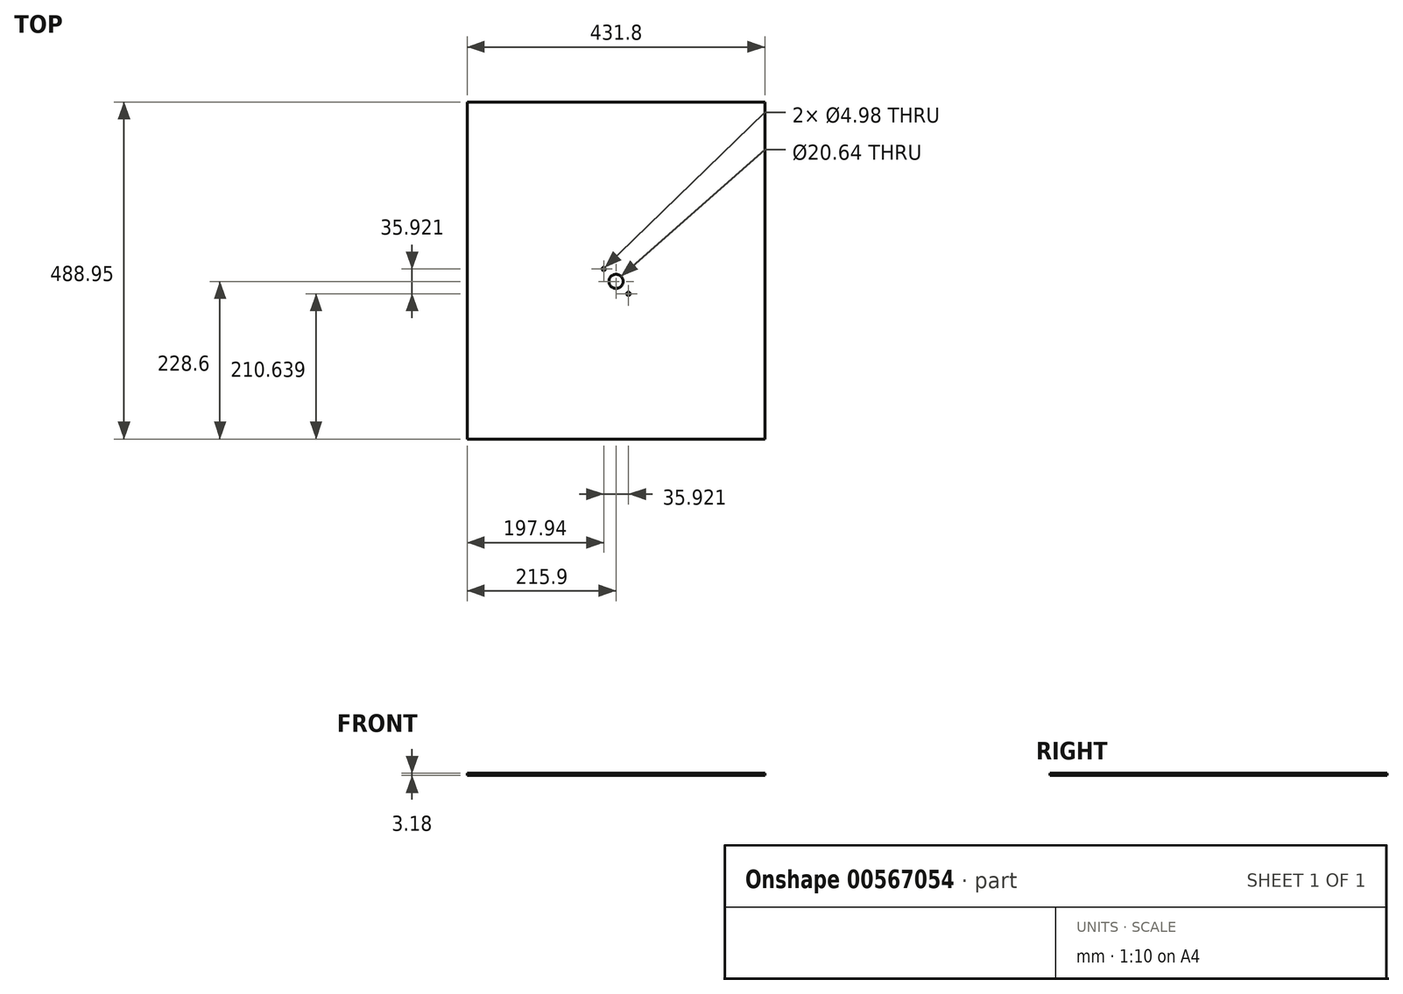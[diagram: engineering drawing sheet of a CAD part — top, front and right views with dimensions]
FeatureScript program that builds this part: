
annotation { "Feature Type Name" : "Feature", "Feature Type Description" : "" }
export const myFeature = defineFeature(function(context is Context, id is Id, definition is map)
    precondition{}
    {
        {
            var Q0;
            Q0=qCreatedBy(makeId("Top.planeOp"),FACE);
            var sketch = newSketch(context, id + "F0", { "sketchPlane" : qUnion([Q0])});
            skPoint(sketch, "E0.middle", {"position": v(0, 15.88) * mm});
            skCircle(sketch, "E1", {"center": v(0, 0) * mm, "radius": 254 * mm, "construction": true});
            skCircle(sketch, "E2", {"center": v(0, 0) * mm, "radius": 10.32 * mm});
            skCircle(sketch, "E3", {"center": v(17.96, -17.96) * mm, "radius": 2.49 * mm});
            skCircle(sketch, "E4", {"center": v(-17.96, 17.96) * mm, "radius": 2.49 * mm});
            skCircle(sketch, "E5", {"center": v(0, 0) * mm, "radius": 25.4 * mm, "construction": true});
            skLineSegment(sketch, "E6", {"start": v(17.96, -17.96) * mm, "end": v(-17.96, 17.96) * mm, "construction": true});
            skLineSegment(sketch, "E7.bottom", {"start": v(-215.9, 260.35) * mm, "end": v(215.9, 260.35) * mm});
            skLineSegment(sketch, "E7.top", {"start": v(-215.9, -228.6) * mm, "end": v(215.9, -228.6) * mm});
            skLineSegment(sketch, "E7.left", {"start": v(-215.9, 260.35) * mm, "end": v(-215.9, -31.75) * mm});
            skLineSegment(sketch, "E7.right", {"start": v(215.9, 260.35) * mm, "end": v(215.9, -228.6) * mm});
            skLineSegment(sketch, "E8", {"start": v(0, -231.78) * mm, "end": v(0, -228.6) * mm, "construction": true});
            skLineSegment(sketch, "E9", {"start": v(0, 260.35) * mm, "end": v(0, 263.53) * mm, "construction": true});
            skLineSegment(sketch, "E10", {"start": v(-219.08, 117.48) * mm, "end": v(-215.9, 117.48) * mm, "construction": true});
            skCircle(sketch, "E11", {"center": v(0, 0) * mm, "radius": 203.2 * mm, "construction": true});
            skLineSegment(sketch, "E12", {"start": v(-215.9, -31.75) * mm, "end": v(-215.9, -228.6) * mm});
            skPoint(sketch, "E13.orphan", {"position": v(219.08, -231.78) * mm});
            skPoint(sketch, "E14.orphan", {"position": v(219.08, 263.53) * mm});
            skPoint(sketch, "E15.orphan", {"position": v(-219.08, 263.53) * mm});
            skPoint(sketch, "E16.end.orphan", {"position": v(219.08, 15.88) * mm});
            skPoint(sketch, "E16.start.orphan", {"position": v(215.9, 15.88) * mm});
            skSolve(sketch);
        }
        {
            var Q0;
            Q0=makeQuery(id+"F0.imprint","IMPRINT",FACE,{"disambiguationData":[TD([[makeQuery(id+"F0.imprint","IMPRINT",EDGE,{"derivedFrom":sQuery(id+"F0.wireOp",EDGE,"E2")}),-1.0]])]});
            extrude(context, id + "F1", {"entities" : qUnion([Q0]), "depth" : 3.17 * mm, "offsetDistance" : 25.4 * mm});
        }
    });
